# Revit family: Shower-Wall-Bradley_Corp-HN300-VL-SR
name_source: partatom
category: Plumbing Fixtures
revit_build: Autodesk Revit MEP 2012 (Build: 20110309_2315(x64)
units: mm (PartAtom-declared; Revit-internal decimal feet)

## types (98) — shared parameters
ADA Compliant = Yes
Assembly Code = D2010710
Buy American Act = To Be Determined
Cold Water Connection Diameter = 1"
Cold Water Connection Radius = 0"
Default Elevation = 48 "
Depth = 36 "
Description = ADA Compliant In-Wall Shower
Height = 80 "
Hot Water Connection Diameter = 1"
Hot Water Connection Radius = 0"
Installation Type = Wall Mounted
Low Emitting Finish = Yes
Low Emitting Material = Yes
Manufacturer = Bradley Corporation
MasterFormat Number = 22 42 23
MasterFormat Title = Commercial Showers
Maximum Operating Pressure = 0.00 psi
Minimum Flow = 0 GPM
OmniClass Table 21 Number = 21-04 20 10 60
OmniClass Table 21 Title = Plumbing Fixtures
OmniClass Table 23 Number = 23-31 17 00
OmniClass Table 23 Title = Showers
Product Tech Data URL - English = http://bradleycorp.com
Seat Material = Plastic - Bradley Corp - Polyethylene - White
Showerhead Height = 72 "
Showerhead Material = Metal - Bradley Corp - Chrome
Specifications URL = http://www.bradleycorp.com
URL = http://www.bradleycorp.com
Valve Material = Metal - Bradley Corp - Chrome
Version = 2.0
Width = 36 "
zero-valued in all types: CWFU, HWFU, Percentage of Recycled Content

## per-type parameters (varying)
| type | Air Metering Valve | CALC_ASTT | CALC_EqPlate | CALC_EqTMV | Deluxe Showerhead with Ball Joint | Economy Soft Flow Showerhead with Ball Joint | Equa-Flo HD Pressure Balancing Valve | Equa-Flo Pressure Balancing Valve | Infrared Metering Valve | Lockable Ball Joint | Model | Optional 1.5 GPM Flow Control | Recessed Soap Dish | Severe Service Showerhead | Single Compression Valve with Lever Handle | Standard Showerhead | Standard Soap Dish | Thermostatic Mixing Valve | TouchTime Metering Valve - 1 Minute | TouchTime Metering Valve - 3 Minute | Type Comments |
| Hot/Tempered and Cold Supplies | No | No | No | No | No | No | No | No | No | No | - | No | No | No | No | No | No | No | No | No | - |
| HN300-VL-SR-EF-S-SD | No | No | Yes | No | No | No | No | Yes | No | No | HN300-VL-SR | No | No | No | No | Yes | Yes | No | No | No | ADA Compliant In-Wall Shower with Equa-Flo Pressure Balancing Valve and Standard Showerhead and Wall-Mount Soap Dish |
| HN300-VL-SR-HD-S-SD | No | No | Yes | Yes | No | No | Yes | No | No | No | HN300-VL-SR | No | No | No | No | Yes | Yes | No | No | No | ADA Compliant In-Wall Shower with Equa-Flo HD Pressure Balancing Valve and Standard Showerhead and Wall-Mount Soap Dish |
| HN300-VL-SR-TMV-S-SD | No | No | Yes | Yes | No | No | No | No | No | No | HN300-VL-SR | No | No | No | No | Yes | Yes | Yes | No | No | ADA Compliant In-Wall Shower with Thermostatic Mixing Valve and Standard Showerhead and Wall-Mount Soap Dish |
| HN300-VL-SR-EF-SX-SD | No | No | Yes | No | No | No | No | Yes | No | No | HN300-VL-SR | No | No | Yes | No | No | Yes | No | No | No | ADA Compliant In-Wall Shower with Equa-Flo Pressure Balancing Valve and Severe Service Showerhead and Wall-Mount Soap Dish |
| HN300-VL-SR-EF-SX-G-SD | No | No | Yes | No | No | No | No | Yes | No | No | HN300-VL-SR | Yes | No | Yes | No | No | Yes | No | No | No | ADA Compliant In-Wall Shower with Equa-Flo Pressure Balancing Valve and Severe Service Showerhead with optional 1.5GPM Flow Control and Wall-Mount Soap Dish |
| HN300-VL-SR-HD-SX-SD | No | No | Yes | Yes | No | No | Yes | No | No | No | HN300-VL-SR | No | No | Yes | No | No | Yes | No | No | No | ADA Compliant In-Wall Shower with Equa-Flo HD Pressure Balancing Valve and Severe Service Showerhead and Wall-Mount Soap Dish |
| HN300-VL-SR-HD-SX-G-SD | No | No | Yes | Yes | No | No | Yes | No | No | No | HN300-VL-SR | Yes | No | Yes | No | No | Yes | No | No | No | ADA Compliant In-Wall Shower with Equa-Flo HD Pressure Balancing Valve and Severe Service Showerhead with optional 1.5GPM Flow Control and Wall-Mount Soap Dish |
| HN300-VL-SR-TMV-SX-SD | No | No | Yes | Yes | No | No | No | No | No | No | HN300-VL-SR | No | No | Yes | No | No | Yes | Yes | No | No | ADA Compliant In-Wall Shower with Thermostatic Mixing Valve and Severe Service Showerhead and Wall-Mount Soap Dish |
| HN300-VL-SR-TMV-SX-G-SD | No | No | Yes | Yes | No | No | No | No | No | No | HN300-VL-SR | Yes | No | Yes | No | No | Yes | Yes | No | No | ADA Compliant In-Wall Shower with Thermostatic Mixing Valve and Severe Service Showerhead with optional 1.5GPM Flow Control and Wall-Mount Soap Dish |
| HN300-VL-SR-EF-SF-SD | No | No | Yes | No | Yes | No | No | Yes | No | No | HN300-VL-SR | No | No | No | No | No | Yes | No | No | No | ADA Compliant In-Wall Shower with Equa-Flo Pressure Balancing Valve and Deluxe Showerhead with Ball Joint and Wall-Mount Soap Dish |
| HN300-VL-SR-EF-SF-LBJ-SD | No | No | Yes | No | Yes | No | No | Yes | No | Yes | HN300-VL-SR | No | No | No | No | No | Yes | No | No | No | ADA Compliant In-Wall Shower with Equa-Flo Pressure Balancing Valve and Deluxe Showerhead with Ball Joint with optional Lockable Ball Joint and Wall-Mount Soap Dish |
| HN300-VL-SR-HD-SF-SD | No | No | Yes | Yes | Yes | No | Yes | No | No | No | HN300-VL-SR | No | No | No | No | No | Yes | No | No | No | ADA Compliant In-Wall Shower with Equa-Flo HD Pressure Balancing Valve and Deluxe Showerhead with Ball Joint and Wall-Mount Soap Dish |
| HN300-VL-SR-HD-SF-LBJ-SD | No | No | Yes | Yes | Yes | No | Yes | No | No | Yes | HN300-VL-SR | No | No | No | No | No | Yes | No | No | No | ADA Compliant In-Wall Shower with Equa-Flo HD Pressure Balancing Valve and Deluxe Showerhead with Ball Joint with optional Lockable Ball Joint and Wall-Mount Soap Dish |
| HN300-VL-SR-TMV-SF-SD | No | No | Yes | Yes | Yes | No | No | No | No | No | HN300-VL-SR | No | No | No | No | No | Yes | Yes | No | No | ADA Compliant In-Wall Shower with Thermostatic Mixing Valve and Deluxe Showerhead with Ball Joint and Wall-Mount Soap Dish |
| HN300-VL-SR-TMV-SF-LBJ-SD | No | No | Yes | Yes | Yes | No | No | No | No | Yes | HN300-VL-SR | No | No | No | No | No | Yes | Yes | No | No | ADA Compliant In-Wall Shower with Thermostatic Mixing Valve and Deluxe Showerhead with Ball Joint with optional Lockable Ball Joint and Wall-Mount Soap Dish |
| HN300-VL-SR-EF-ES-SD | No | No | Yes | No | No | Yes | No | Yes | No | No | HN300-VL-SR | No | No | No | No | No | Yes | No | No | No | ADA Compliant In-Wall Shower with Equa-Flo Pressure Balancing Valve and Economy Soft Flow Showerhead with Ball Joint and Wall-Mount Soap Dish |
| HN300-VL-SR-HD-ES-SD | No | No | Yes | Yes | No | Yes | Yes | No | No | No | HN300-VL-SR | No | No | No | No | No | Yes | No | No | No | ADA Compliant In-Wall Shower with Equa-Flo HD Pressure Balancing Valve and Economy Soft Flow Showerhead with Ball Joint and Wall-Mount Soap Dish |
| HN300-VL-SR-TMV-ES-SD | No | No | Yes | Yes | No | Yes | No | No | No | No | HN300-VL-SR | No | No | No | No | No | Yes | Yes | No | No | ADA Compliant In-Wall Shower with Thermostatic Mixing Valve and Economy Soft Flow Showerhead with Ball Joint and Wall-Mount Soap Dish |
| HN300-VL-SR-EF-S-RSD | No | No | Yes | No | No | No | No | Yes | No | No | HN300-VL-SR | No | Yes | No | No | Yes | No | No | No | No | ADA Compliant In-Wall Shower with Equa-Flo Pressure Balancing Valve and Standard Showerhead and Recessed Soap Dish |
| HN300-VL-SR-HD-S-RSD | No | No | Yes | Yes | No | No | Yes | No | No | No | HN300-VL-SR | No | Yes | No | No | Yes | No | No | No | No | ADA Compliant In-Wall Shower with Equa-Flo HD Pressure Balancing Valve and Standard Showerhead and Recessed Soap Dish |
| HN300-VL-SR-TMV-S-RSD | No | No | Yes | Yes | No | No | No | No | No | No | HN300-VL-SR | No | Yes | No | No | Yes | No | Yes | No | No | ADA Compliant In-Wall Shower with Thermostatic Mixing Valve and Standard Showerhead and Recessed Soap Dish |
| HN300-VL-SR-EF-SX-RSD | No | No | Yes | No | No | No | No | Yes | No | No | HN300-VL-SR | No | Yes | Yes | No | No | No | No | No | No | ADA Compliant In-Wall Shower with Equa-Flo Pressure Balancing Valve and Severe Service Showerhead and Recessed Soap Dish |
| HN300-VL-SR-EF-SX-G-RSD | No | No | Yes | No | No | No | No | Yes | No | No | HN300-VL-SR | Yes | Yes | Yes | No | No | No | No | No | No | ADA Compliant In-Wall Shower with Equa-Flo Pressure Balancing Valve and Severe Service Showerhead with optional 1.5GPM Flow Control and Recessed Soap Dish |
| HN300-VL-SR-HD-SX-RSD | No | No | Yes | Yes | No | No | Yes | No | No | No | HN300-VL-SR | No | Yes | Yes | No | No | No | No | No | No | ADA Compliant In-Wall Shower with Equa-Flo HD Pressure Balancing Valve and Severe Service Showerhead and Recessed Soap Dish |
| HN300-VL-SR-HD-SX-G-RSD | No | No | Yes | Yes | No | No | Yes | No | No | No | HN300-VL-SR | Yes | Yes | Yes | No | No | No | No | No | No | ADA Compliant In-Wall Shower with Equa-Flo HD Pressure Balancing Valve and Severe Service Showerhead with optional 1.5GPM Flow Control and Recessed Soap Dish |
| HN300-VL-SR-TMV-SX-RSD | No | No | Yes | Yes | No | No | No | No | No | No | HN300-VL-SR | No | Yes | Yes | No | No | No | Yes | No | No | ADA Compliant In-Wall Shower with Thermostatic Mixing Valve and Severe Service Showerhead and Recessed Soap Dish |
| HN300-VL-SR-TMV-SX-G-RSD | No | No | Yes | Yes | No | No | No | No | No | No | HN300-VL-SR | Yes | Yes | Yes | No | No | No | Yes | No | No | ADA Compliant In-Wall Shower with Thermostatic Mixing Valve and Severe Service Showerhead with optional 1.5GPM Flow Control and Recessed Soap Dish |
| HN300-VL-SR-EF-SF-RSD | No | No | Yes | No | Yes | No | No | Yes | No | No | HN300-VL-SR | No | Yes | No | No | No | No | No | No | No | ADA Compliant In-Wall Shower with Equa-Flo Pressure Balancing Valve and Deluxe Showerhead with Ball Joint and Recessed Soap Dish |
| HN300-VL-SR-EF-SF-LBJ-RSD | No | No | Yes | No | Yes | No | No | Yes | No | Yes | HN300-VL-SR | No | Yes | No | No | No | No | No | No | No | ADA Compliant In-Wall Shower with Equa-Flo Pressure Balancing Valve and Deluxe Showerhead with Ball Joint with optional Lockable Ball Joint and Recessed Soap Dish |
| HN300-VL-SR-HD-SF-RSD | No | No | Yes | Yes | Yes | No | Yes | No | No | No | HN300-VL-SR | No | Yes | No | No | No | No | No | No | No | ADA Compliant In-Wall Shower with Equa-Flo HD Pressure Balancing Valve and Deluxe Showerhead with Ball Joint and Recessed Soap Dish |
| HN300-VL-SR-HD-SF-LBJ-RSD | No | No | Yes | Yes | Yes | No | Yes | No | No | Yes | HN300-VL-SR | No | Yes | No | No | No | No | No | No | No | ADA Compliant In-Wall Shower with Equa-Flo HD Pressure Balancing Valve and Deluxe Showerhead with Ball Joint with optional Lockable Ball Joint and Recessed Soap Dish |
| HN300-VL-SR-TMV-SF-RSD | No | No | Yes | Yes | Yes | No | No | No | No | No | HN300-VL-SR | No | Yes | No | No | No | No | Yes | No | No | ADA Compliant In-Wall Shower with Thermostatic Mixing Valve and Deluxe Showerhead with Ball Joint and Recessed Soap Dish |
| HN300-VL-SR-TMV-SF-LBJ-RSD | No | No | Yes | Yes | Yes | No | No | No | No | Yes | HN300-VL-SR | No | Yes | No | No | No | No | Yes | No | No | ADA Compliant In-Wall Shower with Thermostatic Mixing Valve and Deluxe Showerhead with Ball Joint with optional Lockable Ball Joint and Recessed Soap Dish |
| HN300-VL-SR-EF-ES-RSD | No | No | Yes | No | No | Yes | No | Yes | No | No | HN300-VL-SR | No | Yes | No | No | No | No | No | No | No | ADA Compliant In-Wall Shower with Equa-Flo Pressure Balancing Valve and Economy Soft Flow Showerhead with Ball Joint and Recessed Soap Dish |
| HN300-VL-SR-HD-ES-RSD | No | No | Yes | Yes | No | Yes | Yes | No | No | No | HN300-VL-SR | No | Yes | No | No | No | No | No | No | No | ADA Compliant In-Wall Shower with Equa-Flo HD Pressure Balancing Valve and Economy Soft Flow Showerhead with Ball Joint and Recessed Soap Dish |
| HN300-VL-SR-TMV-ES-RSD | No | No | Yes | Yes | No | Yes | No | No | No | No | HN300-VL-SR | No | Yes | No | No | No | No | Yes | No | No | ADA Compliant In-Wall Shower with Thermostatic Mixing Valve and Economy Soft Flow Showerhead with Ball Joint and Recessed Soap Dish |
| Single Tempered/Cold Supply | No | No | No | No | No | No | No | No | No | No | - | No | No | No | No | No | No | No | No | No | - |
| HN300-VL-SR-AZ-S-SD | No | No | No | No | No | No | No | No | Yes | No | HN300-VL-SR | No | No | No | No | Yes | Yes | No | No | No | ADA Compliant In-Wall Shower with Infrared Metering Valve and Standard Showerhead and Wall-Mount Soap Dish |
| HN300-VL-SR-AZ-SX-SD | No | No | No | No | No | No | No | No | Yes | No | HN300-VL-SR | No | No | Yes | No | No | Yes | No | No | No | ADA Compliant In-Wall Shower with Infrared Metering Valve and Severe Service Showerhead and Wall-Mount Soap Dish |
| HN300-VL-SR-AZ-SX-G-SD | No | No | No | No | No | No | No | No | Yes | No | HN300-VL-SR | Yes | No | Yes | No | No | Yes | No | No | No | ADA Compliant In-Wall Shower with Infrared Metering Valve and Severe Service Showerhead with optional 1.5GPM Flow Control and Wall-Mount Soap Dish |
| HN300-VL-SR-AZ-SF-SD | No | No | No | No | Yes | No | No | No | Yes | No | HN300-VL-SR | No | No | No | No | No | Yes | No | No | No | ADA Compliant In-Wall Shower with Infrared Metering Valve and Deluxe Showerhead with Ball Joint and Wall-Mount Soap Dish |
| HN300-VL-SR-AZ-SF-LBJ-SD | No | No | No | No | Yes | No | No | No | Yes | Yes | HN300-VL-SR | No | No | No | No | No | Yes | No | No | No | ADA Compliant In-Wall Shower with Infrared Metering Valve and Deluxe Showerhead with Ball Joint with optional Lockable Ball Joint and Wall-Mount Soap Dish |
| HN300-VL-SR-AZ-ES-SD | No | No | No | No | No | Yes | No | No | Yes | No | HN300-VL-SR | No | No | No | No | No | Yes | No | No | No | ADA Compliant In-Wall Shower with Infrared Metering Valve and Economy Soft Flow Showerhead with Ball Joint and Wall-Mount Soap Dish |
| HN300-VL-SR-AST-S-SD | Yes | Yes | No | No | No | No | No | No | No | No | HN300-VL-SR | No | No | No | No | Yes | Yes | No | No | No | ADA Compliant In-Wall Shower with Air Metering Valve and Standard Showerhead and Wall-Mount Soap Dish |
| HN300-VL-SR-AST-SX-SD | Yes | Yes | No | No | No | No | No | No | No | No | HN300-VL-SR | No | No | Yes | No | No | Yes | No | No | No | ADA Compliant In-Wall Shower with Air Metering Valve and Severe Service Showerhead and Wall-Mount Soap Dish |
| HN300-VL-SR-AST-SX-G-SD | Yes | Yes | No | No | No | No | No | No | No | No | HN300-VL-SR | Yes | No | Yes | No | No | Yes | No | No | No | ADA Compliant In-Wall Shower with Air Metering Valve and Severe Service Showerhead with optional 1.5GPM Flow Control and Wall-Mount Soap Dish |
| HN300-VL-SR-AST-SF-SD | Yes | Yes | No | No | Yes | No | No | No | No | No | HN300-VL-SR | No | No | No | No | No | Yes | No | No | No | ADA Compliant In-Wall Shower with Air Metering Valve and Deluxe Showerhead with Ball Joint and Wall-Mount Soap Dish |
| HN300-VL-SR-AST-SF-LBJ-SD | Yes | Yes | No | No | Yes | No | No | No | No | Yes | HN300-VL-SR | No | No | No | No | No | Yes | No | No | No | ADA Compliant In-Wall Shower with Air Metering Valve and Deluxe Showerhead with Ball Joint with optional Lockable Ball Joint and Wall-Mount Soap Dish |
| HN300-VL-SR-AST-ES-SD | Yes | Yes | No | No | No | Yes | No | No | No | No | HN300-VL-SR | No | No | No | No | No | Yes | No | No | No | ADA Compliant In-Wall Shower with Air Metering Valve and Economy Soft Flow Showerhead with Ball Joint and Wall-Mount Soap Dish |
| HN300-VL-SR-SVL-S-SD | No | No | No | No | No | No | No | No | No | No | HN300-VL-SR | No | No | No | Yes | Yes | Yes | No | No | No | ADA Compliant In-Wall Shower with Single Compression Valve and Standard Showerhead and Wall-Mount Soap Dish |
| HN300-VL-SR-SVL-SX-SD | No | No | No | No | No | No | No | No | No | No | HN300-VL-SR | No | No | Yes | Yes | No | Yes | No | No | No | ADA Compliant In-Wall Shower with Single Compression Valve and Severe Service Showerhead and Wall-Mount Soap Dish |
| HN300-VL-SR-SVL-SX-G-SD | No | No | No | No | No | No | No | No | No | No | HN300-VL-SR | Yes | No | Yes | Yes | No | Yes | No | No | No | ADA Compliant In-Wall Shower with Single Compression Valve and Severe Service Showerhead with optional 1.5GPM Flow Control and Wall-Mount Soap Dish |
| HN300-VL-SR-SVL-SF-SD | No | No | No | No | Yes | No | No | No | No | No | HN300-VL-SR | No | No | No | Yes | No | Yes | No | No | No | ADA Compliant In-Wall Shower with Single Compression Valve and Deluxe Showerhead with Ball Joint and Wall-Mount Soap Dish |
| HN300-VL-SR-SVL-SF-LBJ-SD | No | No | No | No | Yes | No | No | No | No | Yes | HN300-VL-SR | No | No | No | Yes | No | Yes | No | No | No | ADA Compliant In-Wall Shower with Single Compression Valve and Deluxe Showerhead with Ball Joint with optional Lockable Ball Joint and Wall-Mount Soap Dish |
| HN300-VL-SR-SVL-ES-SD | No | No | No | No | No | Yes | No | No | No | No | HN300-VL-SR | No | No | No | Yes | No | Yes | No | No | No | ADA Compliant In-Wall Shower with Single Compression Valve and Economy Soft Flow Showerhead wiht Ball Joint and Wall-Mount Soap Dish |
| HN300-VL-SR-TT-S-SD | No | Yes | No | No | No | No | No | No | No | No | HN300-VL-SR | No | No | No | No | Yes | Yes | No | Yes | No | ADA Compliant In-Wall Shower with TouchTime Metering Valve - 1 Minute and Standard Showerhead and Wall-Mount Soap Dish |
| HN300-VL-SR-TT-SX-SD | No | Yes | No | No | No | No | No | No | No | No | HN300-VL-SR | No | No | Yes | No | No | Yes | No | Yes | No | ADA Compliant In-Wall Shower with TouchTime Metering Valve - 1 Minute and Severe Service Showerhead and Wall-Mount Soap Dish |
| HN300-VL-SR-TT-SX-G-SD | No | Yes | No | No | No | No | No | No | No | No | HN300-VL-SR | Yes | No | Yes | No | No | Yes | No | Yes | No | ADA Compliant In-Wall Shower with TouchTime Metering Valve - 1 Minute and Severe Service Showerhead with optional 1.5GPM Flow Control and Wall-Mount Soap Dish |
| HN300-VL-SR-TT-SF-SD | No | Yes | No | No | Yes | No | No | No | No | No | HN300-VL-SR | No | No | No | No | No | Yes | No | Yes | No | ADA Compliant In-Wall Shower with TouchTime Metering Valve - 1 Minute and Deluxe Showerhead with Ball Joint and Wall-Mount Soap Dish |
| HN300-VL-SR-TT-SF-LBJ-SD | No | Yes | No | No | Yes | No | No | No | No | Yes | HN300-VL-SR | No | No | No | No | No | Yes | No | Yes | No | ADA Compliant In-Wall Shower with TouchTime Metering Valve - 1 Minute and Deluxe Showerhead with Ball Joint with optional Lockable Ball Joint and Wall-Mount Soap Dish |
| HN300-VL-SR-TT-ES-SD | No | Yes | No | No | No | Yes | No | No | No | No | HN300-VL-SR | No | No | No | No | No | Yes | No | Yes | No | ADA Compliant In-Wall Shower with TouchTime Metering Valve - 1 Minute and Economy Soft Flow Showerhead wiht Ball Joint and Wall-Mount Soap Dish |
| HN300-VL-SR-TT3-S-SD | No | Yes | No | No | No | No | No | No | No | No | HN300-VL-SR | No | No | No | No | Yes | Yes | No | No | Yes | ADA Compliant In-Wall Shower with TouchTime Metering Valve - 3 Minute and Standard Showerhead and Wall-Mount Soap Dish |
| HN300-VL-SR-TT3-SX-SD | No | Yes | No | No | No | No | No | No | No | No | HN300-VL-SR | No | No | Yes | No | No | Yes | No | No | Yes | ADA Compliant In-Wall Shower with TouchTime Metering Valve - 3 Minute and Severe Service Showerhead and Wall-Mount Soap Dish |
| HN300-VL-SR-TT3-SX-G-SD | No | Yes | No | No | No | No | No | No | No | No | HN300-VL-SR | Yes | No | Yes | No | No | Yes | No | No | Yes | ADA Compliant In-Wall Shower with TouchTime Metering Valve - 3 Minute and Severe Service Showerhead with optional 1.5GPM Flow Control and Wall-Mount Soap Dish |
| HN300-VL-SR-TT3-SF-SD | No | Yes | No | No | Yes | No | No | No | No | No | HN300-VL-SR | No | No | No | No | No | Yes | No | No | Yes | ADA Compliant In-Wall Shower with TouchTime Metering Valve - 3 Minute and Deluxe Showerhead with Ball Joint and Wall-Mount Soap Dish |
| HN300-VL-SR-TT3-SF-LBJ-SD | No | Yes | No | No | Yes | No | No | No | No | Yes | HN300-VL-SR | No | No | No | No | No | Yes | No | No | Yes | ADA Compliant In-Wall Shower with TouchTime Metering Valve - 3 Minute and Deluxe Showerhead with Ball Joint with optional Lockable Ball Joint and Wall-Mount Soap Dish |
| HN300-VL-SR-TT3-ES-SD | No | Yes | No | No | No | Yes | No | No | No | No | HN300-VL-SR | No | No | No | No | No | Yes | No | No | Yes | ADA Compliant In-Wall Shower with TouchTime Metering Valve - 3 Minute and Economy Soft Flow Showerhead wiht Ball Joint and Wall-Mount Soap Dish |
| HN300-VL-SR-AZ-S-RSD | No | No | No | No | No | No | No | No | Yes | No | HN300-VL-SR | No | Yes | No | No | Yes | No | No | No | No | ADA Compliant In-Wall Shower with Infrared Metering Valve and Standard Showerhead and Recessed Soap Dish |
| HN300-VL-SR-AZ-SX-RSD | No | No | No | No | No | No | No | No | Yes | No | HN300-VL-SR | No | Yes | Yes | No | No | No | No | No | No | ADA Compliant In-Wall Shower with Infrared Metering Valve and Severe Service Showerhead and Recessed Soap Dish |
| HN300-VL-SR-AZ-SX-G-RSD | No | No | No | No | No | No | No | No | Yes | No | HN300-VL-SR | Yes | Yes | Yes | No | No | No | No | No | No | ADA Compliant In-Wall Shower with Infrared Metering Valve and Severe Service Showerhead with optional 1.5GPM Flow Control and Recessed Soap Dish |
| HN300-VL-SR-AZ-SF-RSD | No | No | No | No | Yes | No | No | No | Yes | No | HN300-VL-SR | No | Yes | No | No | No | No | No | No | No | ADA Compliant In-Wall Shower with Infrared Metering Valve and Deluxe Showerhead with Ball Joint and Recessed Soap Dish |
| HN300-VL-SR-AZ-SF-LBJ-RSD | No | No | No | No | Yes | No | No | No | Yes | Yes | HN300-VL-SR | No | Yes | No | No | No | No | No | No | No | ADA Compliant In-Wall Shower with Infrared Metering Valve and Deluxe Showerhead with Ball Joint with optional Lockable Ball Joint and Recessed Soap Dish |
| HN300-VL-SR-AZ-ES-RSD | No | No | No | No | No | Yes | No | No | Yes | No | HN300-VL-SR | No | Yes | No | No | No | No | No | No | No | ADA Compliant In-Wall Shower with Infrared Metering Valve and Economy Soft Flow Showerhead with Ball Joint and Recessed Soap Dish |
| HN300-VL-SR-AST-S-RSD | Yes | Yes | No | No | No | No | No | No | No | No | HN300-VL-SR | No | Yes | No | No | Yes | No | No | No | No | ADA Compliant In-Wall Shower with Air Metering Valve and Standard Showerhead and Recessed Soap Dish |
| HN300-VL-SR-AST-SX-RSD | Yes | Yes | No | No | No | No | No | No | No | No | HN300-VL-SR | No | Yes | Yes | No | No | No | No | No | No | ADA Compliant In-Wall Shower with Air Metering Valve and Severe Service Showerhead and Recessed Soap Dish |
| HN300-VL-SR-AST-SX-G-RSD | Yes | Yes | No | No | No | No | No | No | No | No | HN300-VL-SR | Yes | Yes | Yes | No | No | No | No | No | No | ADA Compliant In-Wall Shower with Air Metering Valve and Severe Service Showerhead with optional 1.5GPM Flow Control and Recessed Soap Dish |
| HN300-VL-SR-AST-SF-RSD | Yes | Yes | No | No | Yes | No | No | No | No | No | HN300-VL-SR | No | Yes | No | No | No | No | No | No | No | ADA Compliant In-Wall Shower with Air Metering Valve and Deluxe Showerhead with Ball Joint and Recessed Soap Dish |
| HN300-VL-SR-AST-SF-LBJ-RSD | Yes | Yes | No | No | Yes | No | No | No | No | Yes | HN300-VL-SR | No | Yes | No | No | No | No | No | No | No | ADA Compliant In-Wall Shower with Air Metering Valve and Deluxe Showerhead with Ball Joint with optional Lockable Ball Joint and Recessed Soap Dish |
| HN300-VL-SR-AST-ES-RSD | Yes | Yes | No | No | No | Yes | No | No | No | No | HN300-VL-SR | No | Yes | No | No | No | No | No | No | No | ADA Compliant In-Wall Shower with Air Metering Valve and Economy Soft Flow Showerhead with Ball Joint and Recessed Soap Dish |
| HN300-VL-SR-SVL-S-RSD | No | No | No | No | No | No | No | No | No | No | HN300-VL-SR | No | Yes | No | Yes | Yes | No | No | No | No | ADA Compliant In-Wall Shower with Single Compression Valve and Standard Showerhead and Recessed Soap Dish |
| HN300-VL-SR-SVL-SX-RSD | No | No | No | No | No | No | No | No | No | No | HN300-VL-SR | No | Yes | Yes | Yes | No | No | No | No | No | ADA Compliant In-Wall Shower with Single Compression Valve and Severe Service Showerhead and Recessed Soap Dish |
| HN300-VL-SR-SVL-SX-G-RSD | No | No | No | No | No | No | No | No | No | No | HN300-VL-SR | Yes | Yes | Yes | Yes | No | No | No | No | No | ADA Compliant In-Wall Shower with Single Compression Valve and Severe Service Showerhead with optional 1.5GPM Flow Control and Recessed Soap Dish |
| HN300-VL-SR-SVL-SF-RSD | No | No | No | No | Yes | No | No | No | No | No | HN300-VL-SR | No | Yes | No | Yes | No | No | No | No | No | ADA Compliant In-Wall Shower with Single Compression Valve and Deluxe Showerhead with Ball Joint and Recessed Soap Dish |
| HN300-VL-SR-SVL-SF-LBJ-RSD | No | No | No | No | Yes | No | No | No | No | Yes | HN300-VL-SR | No | Yes | No | Yes | No | No | No | No | No | ADA Compliant In-Wall Shower with Single Compression Valve and Deluxe Showerhead with Ball Joint with optional Lockable Ball Joint and Recessed Soap Dish |
| HN300-VL-SR-SVL-ES-RSD | No | No | No | No | No | Yes | No | No | No | No | HN300-VL-SR | No | Yes | No | Yes | No | No | No | No | No | ADA Compliant In-Wall Shower with Single Compression Valve and Economy Soft Flow Showerhead wiht Ball Joint and Recessed Soap Dish |
| HN300-VL-SR-TT-S-RSD | No | Yes | No | No | No | No | No | No | No | No | HN300-VL-SR | No | Yes | No | No | Yes | No | No | Yes | No | ADA Compliant In-Wall Shower with TouchTime Metering Valve - 1 Minute and Standard Showerhead and Recessed Soap Dish |
| HN300-VL-SR-TT-SX-RSD | No | Yes | No | No | No | No | No | No | No | No | HN300-VL-SR | No | Yes | Yes | No | No | No | No | Yes | No | ADA Compliant In-Wall Shower with TouchTime Metering Valve - 1 Minute and Severe Service Showerhead and Recessed Soap Dish |
| HN300-VL-SR-TT-SX-G-RSD | No | Yes | No | No | No | No | No | No | No | No | HN300-VL-SR | Yes | Yes | Yes | No | No | No | No | Yes | No | ADA Compliant In-Wall Shower with TouchTime Metering Valve - 1 Minute and Severe Service Showerhead with optional 1.5GPM Flow Control and Recessed Soap Dish |
| HN300-VL-SR-TT-SF-RSD | No | Yes | No | No | Yes | No | No | No | No | No | HN300-VL-SR | No | Yes | No | No | No | No | No | Yes | No | ADA Compliant In-Wall Shower with TouchTime Metering Valve - 1 Minute and Deluxe Showerhead with Ball Joint and Recessed Soap Dish |
| HN300-VL-SR-TT-SF-LBJ-RSD | No | Yes | No | No | Yes | No | No | No | No | Yes | HN300-VL-SR | No | Yes | No | No | No | No | No | Yes | No | ADA Compliant In-Wall Shower with TouchTime Metering Valve - 1 Minute and Deluxe Showerhead with Ball Joint with optional Lockable Ball Joint and Recessed Soap Dish |
| HN300-VL-SR-TT-ES-RSD | No | Yes | No | No | No | Yes | No | No | No | No | HN300-VL-SR | No | Yes | No | No | No | No | No | Yes | No | ADA Compliant In-Wall Shower with TouchTime Metering Valve - 1 Minute and Economy Soft Flow Showerhead wiht Ball Joint and Recessed Soap Dish |
| HN300-VL-SR-TT3-S-RSD | No | Yes | No | No | No | No | No | No | No | No | HN300-VL-SR | No | Yes | No | No | Yes | No | No | No | Yes | ADA Compliant In-Wall Shower with TouchTime Metering Valve - 3 Minute and Standard Showerhead and Recessed Soap Dish |
| HN300-VL-SR-TT3-SX-RSD | No | Yes | No | No | No | No | No | No | No | No | HN300-VL-SR | No | Yes | Yes | No | No | No | No | No | Yes | ADA Compliant In-Wall Shower with TouchTime Metering Valve - 3 Minute and Severe Service Showerhead and Recessed Soap Dish |
| HN300-VL-SR-TT3-SX-G-RSD | No | Yes | No | No | No | No | No | No | No | No | HN300-VL-SR | Yes | Yes | Yes | No | No | No | No | No | Yes | ADA Compliant In-Wall Shower with TouchTime Metering Valve - 3 Minute and Severe Service Showerhead with optional 1.5GPM Flow Control and Recessed Soap Dish |
| HN300-VL-SR-TT3-SF-RSD | No | Yes | No | No | Yes | No | No | No | No | No | HN300-VL-SR | No | Yes | No | No | No | No | No | No | Yes | ADA Compliant In-Wall Shower with TouchTime Metering Valve - 3 Minute and Deluxe Showerhead with Ball Joint and Recessed Soap Dish |
| HN300-VL-SR-TT3-SF-LBJ-RSD | No | Yes | No | No | Yes | No | No | No | No | Yes | HN300-VL-SR | No | Yes | No | No | No | No | No | No | Yes | ADA Compliant In-Wall Shower with TouchTime Metering Valve - 3 Minute and Deluxe Showerhead with Ball Joint with optional Lockable Ball Joint and Recessed Soap Dish |
| HN300-VL-SR-TT3-ES-RSD | No | Yes | No | No | No | Yes | No | No | No | No | HN300-VL-SR | No | Yes | No | No | No | No | No | No | Yes | ADA Compliant In-Wall Shower with TouchTime Metering Valve - 3 Minute and Economy Soft Flow Showerhead wiht Ball Joint and Recessed Soap Dish |

## geometry (parser evidence)
native form markers: Blend x10, Sweep x9
no freeform markers — native parametric forms only
